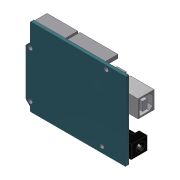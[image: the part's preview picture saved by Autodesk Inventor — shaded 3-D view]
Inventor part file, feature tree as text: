
AUTODESK INVENTOR PART (.ipt)
format: ipt  version: 2014 (Build 180170000, 170)  size: 454,144 bytes
history: native  units: mm
features: sketch x18, extrude x17, hole x1
ambient origin geometry x8: Origin, YZ Plane, XZ Plane, XY Plane, X Axis, Y Axis, Z Axis, Center Point
bodies: Solid1 (feature_tree)
feature tree (36):
  extrude  "Extrusion1"  Depth=3.0mm
  extrude  "Extrusion2"  Depth=3.0mm
  extrude  "Extrusion3"  Depth=65.5mm
  extrude  "Extrusion4"  Depth=38.0mm
  extrude  "Extrusion5"  Depth=0.5mm
  extrude  "Extrusion6"  Depth=6.2mm
  extrude  "Extrusion7"  Depth=2.0mm TaperAngle=0.0deg
  hole  "Hole1"  [1 undecoded]
  extrude  "Extrusion8"  Depth=0.8mm
  extrude  "Extrusion9"  Depth=0.8mm
  extrude  "Extrusion10"  Depth=2.0mm
  extrude  "Extrusion11"  Depth=0.02mm TaperAngle=90.0deg
  extrude  "Extrusion12"  Depth=16.3mm
  extrude  "Extrusion13"  Depth=11.0mm TaperAngle=0.0deg
  extrude  "Extrusion14"  Depth=1.0mm
  extrude  "Extrusion15"  Depth=7.0mm
  extrude  "Extrusion16"  Depth=9.0mm TaperAngle=0.0deg
  extrude  "Extrusion17"  Depth=3.2mm
  sketch  "Sketch1"  dims[d1=53.5mm d3=3.0mm]
  sketch  "Sketch2"  dims[d5=6.0mm d6=3.0mm]
  sketch  "Sketch3"  dims[d7=12.5mm d9=65.5mm]
  sketch  "Sketch4"  dims[d10=65.5mm d11=38.0mm]
  sketch  "Sketch5"  dims[d12=32.0mm d13=0.5mm]
  sketch  "Sketch6"  dims[d14=2.0mm d15=0.0mm d16=6.2mm]
  sketch  "Sketch7"  dims[d17=6.2mm d18=2.0mm d19=0.0mm]
  sketch  "Sketch8"  dims[d20=3.14mm d21=1.5mm d22=0.0mm]
  sketch  "Sketch9"  dims[d23=2.0mm d24=0.8mm]
  sketch  "Sketch10"  dims[d25=2.0mm d26=0.8mm]
  sketch  "Sketch11"  dims[d27=0.8mm d28=2.0mm]
  sketch  "Sketch12"  dims[d29=0.02mm d30=90.0deg d31=0.02mm]
  sketch  "Sketch13"  dims[d32=0.4mm d33=0.0mm d34=16.3mm]
  sketch  "Sketch14"  dims[d35=12.0mm d36=11.0mm d37=0.0mm]
  sketch  "Sketch15"  dims[d39=1.0mm d40=1.0mm]
  sketch  "Sketch16"  dims[d41=10.0mm d43=7.0mm]
  sketch  "Sketch17"  dims[d44=6.0mm d45=9.0mm d46=0.0mm]
  sketch  "Sketch18"  dims[d47=6.0mm d48=3.2mm d49=9.0mm d50=0.0mm d51=3.0mm d52=3.0mm d53=3.0mm d54=3.0mm d55=3.0mm d56=6.0mm d57=4.0mm d58=2.0mm d59=90.0deg d60=8.0mm d61=20.594885mm d62=13.6mm d63=9.0mm d64=11.0mm d65=0.0mm d66=6.0mm d67=8.0mm d68=0.0mm d69=8.0mm d70=0.0mm d71=1.2mm d72=8.0mm d73=0.0mm d74=21.0mm d75=2.5mm d76=26.0mm d77=9.0mm d78=0.0mm d79=2.5mm d80=13.5mm d81=0.75mm d82=1.0mm d83=80.0mm d85=2.65mm d86=10.0mm d88=10.0mm d90=1.0mm d91=0.0mm d92=0.75mm d93=1.0mm d94=100.0mm d96=2.61mm d97=10.0mm d99=10.0mm d101=1.0mm d102=0.0mm d103=15.3mm d104=2.5mm d105=21.0mm d106=9.0mm d107=0.0mm d108=0.75mm d109=1.0mm d110=80.0mm d112=2.65mm d113=10.0mm d115=10.0mm d117=1.0mm d118=0.0mm d119=0.75mm d120=1.0mm d121=60.0mm d123=2.6mm d124=10.0mm d126=10.0mm d128=1.0mm d129=0.0mm]
note: 1 required parameter value undecoded (feature->parameter linkage not recoverable at this tier; creation-order binding heuristic only, values carry confidence <= 0.55)
